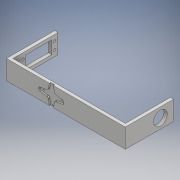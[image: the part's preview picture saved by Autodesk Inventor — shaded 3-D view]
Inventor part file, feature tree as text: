
AUTODESK INVENTOR PART (.ipt)
format: ipt  version: 2018 (Build 220112000, 112)  size: 218,624 bytes
history: native  units: mm
features: extrude x5, sketch x4
ambient origin geometry x8: Origin, YZ Plane, XZ Plane, XY Plane, X Axis, Y Axis, Z Axis, Center Point
bodies: Solid1 (feature_tree)
feature tree (9):
  extrude  "Extrusion1"  Depth=70.0mm
  extrude  "Extrusion2"  Depth=75.0mm
  extrude  "Extrusion3"  Depth=75.0mm
  sketch  "Sketch4"  dims[d6=5.0mm d7=30.0mm d8=0.0mm d9=30.0mm d10=20.0mm d11=41.0mm d12=4.0mm d13=4.0mm d14=4.0mm d15=4.0mm d16=4.0mm d17=4.0mm d18=4.0mm d19=4.0mm d20=4.0mm d21=4.0mm d22=4.0mm d23=4.0mm d24=10.0mm d25=0.0mm d26=11.0mm d27=21.5mm d28=14.5mm d29=0.0mm d35=2.0mm d37=1.745329mm d39=1.745329mm d41=1.745329mm d43=1.745329mm d45=1.745329mm d47=1.745329mm d49=1.745329mm d51=1.745329mm d52=2.0mm d53=2.0mm d54=70.0mm d55=6.5mm d56=6.5mm d57=14.0mm d58=14.0mm d59=14.0mm d60=14.0mm d61=1.5mm d62=1.5mm d63=1.5mm d64=1.5mm d65=2.0mm d66=0.0mm d67=22.0mm d68=0.0mm]
  extrude  "Extrusion4"  Depth=30.0mm TaperAngle=0.0deg
  extrude  "Extrusion5"  Depth=30.0mm
  sketch  "Sketch1"  dims[d0=175.0mm d1=70.0mm]
  sketch  "Sketch2"  dims[d2=5.0mm d3=75.0mm]
  sketch  "Sketch3"  dims[d4=185.0mm d5=75.0mm]
